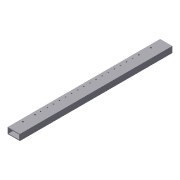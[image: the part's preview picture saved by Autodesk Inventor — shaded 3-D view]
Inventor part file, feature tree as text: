
AUTODESK INVENTOR PART (.ipt)
format: ipt  version: 2012 (Build 160160000, 160)  size: 143,360 bytes
history: native  units: in
note: dims shown in document units (in); Inventor stores cm internally (conversion verified against a paired STEP export)
features: extrude x3, sketch x3, shell x1
ambient origin geometry x8: Origin, YZ Plane, XZ Plane, XY Plane, X Axis, Y Axis, Z Axis, Center Point
bodies: Solid1 (feature_tree)
feature tree (7):
  extrude  "Extrusion1"  Depth=2.0in
  shell  "Shell1"  Thickness=25.0in
  extrude  "Extrusion2"  Depth=2.0in
  extrude  "Extrusion3"  Depth=0.25in
  sketch  "Sketch1"  dims[d0=1.0in d1=2.0in d2=25.0in d3=0.0in]
  sketch  "Sketch2"  dims[d4=0.5in d5=2.0in]
  sketch  "Sketch3"  dims[d6=2.0in d7=0.25in d8=0.25in d9=0.25in d10=0.25in d11=25.0in d12=0.0in d13=0.125in d14=0.5in d15=1.0in d16=5.0in d17=0.1875in d18=25.0in d19=0.0in]
